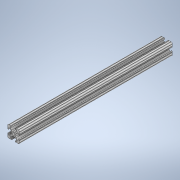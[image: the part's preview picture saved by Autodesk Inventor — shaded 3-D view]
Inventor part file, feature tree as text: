
AUTODESK INVENTOR PART (.ipt)
format: ipt  version: 2020 (Build 240168000, 168)  size: 235,520 bytes
history: native  units: in
note: dims shown in document units (in); Inventor stores cm internally (conversion verified against a paired STEP export)
features: extrude x1, sketch x1
ambient origin geometry x8: Origin, YZ Plane, XZ Plane, XY Plane, X Axis, Y Axis, Z Axis, Center Point
bodies: Solid1 (feature_tree)
feature tree (2):
  extrude  "Extrusion1"  [1 undecoded]
  sketch  "Sketch1"  dims[d0=13.0in d1=0.0in]
note: 1 required parameter value undecoded (feature->parameter linkage not recoverable at this tier; creation-order binding heuristic only, values carry confidence <= 0.55)
